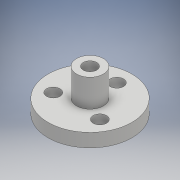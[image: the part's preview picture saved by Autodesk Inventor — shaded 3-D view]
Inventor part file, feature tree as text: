
AUTODESK INVENTOR PART (.ipt)
format: ipt  version: 2018 (Build 220112000, 112)  size: 118,784 bytes
history: native  units: mm
features: extrude x2, sketch x1
ambient origin geometry x8: Origin, YZ Plane, XZ Plane, XY Plane, X Axis, Y Axis, Z Axis, Center Point
bodies: Solid1 (feature_tree)
feature tree (3):
  sketch  "Sketch1"  dims[d0=26.5mm d1=4.25mm d2=8.5mm d3=0.0mm d4=4.25mm d5=8.5mm d6=30.0mm d8=360.0deg d10=4.25mm d11=0.0mm d12=13.0mm d13=0.0mm]
  extrude  "Extrusion1"  Depth=4.25mm
  extrude  "Extrusion2"  Depth=8.5mm
